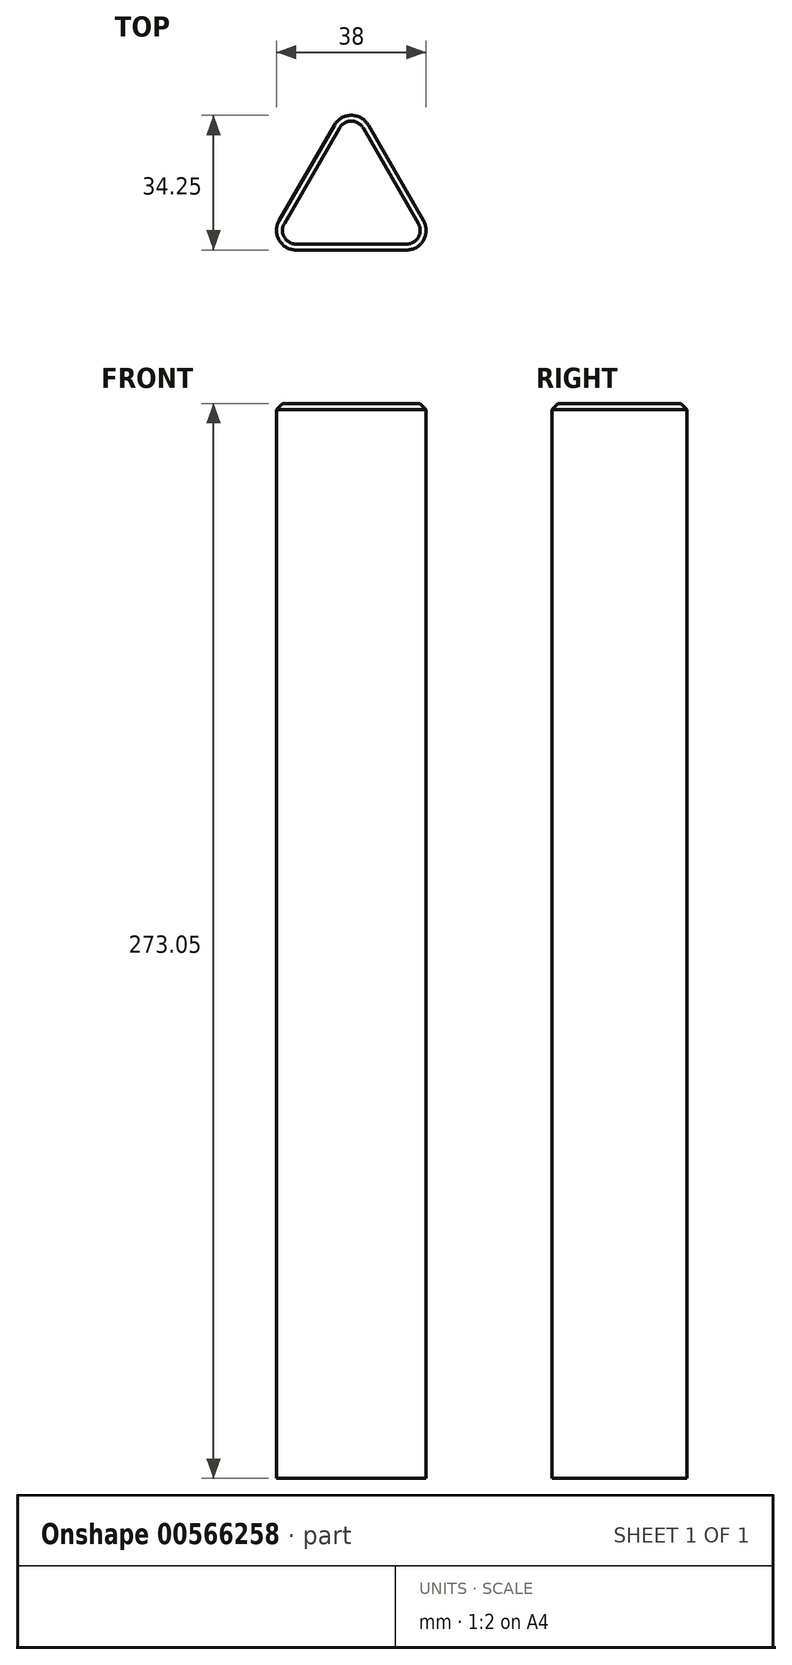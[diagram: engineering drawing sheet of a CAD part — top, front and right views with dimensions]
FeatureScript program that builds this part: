
annotation { "Feature Type Name" : "Feature", "Feature Type Description" : "" }
export const myFeature = defineFeature(function(context is Context, id is Id, definition is map)
    precondition{}
    {
        {
            assignVariable(context, id + "F0", {"variableType" : VariableType.LENGTH, "name" : "height1", "lengthValue" : 273.05 * mm});
        }
        {
            var Q0;
            Q0=qCreatedBy(makeId("Top.planeOp"),FACE);
            var sketch = newSketch(context, id + "F1", { "sketchPlane" : qUnion([Q0])});
            skLineSegment(sketch, "E0", {"start": v(4.33, 18.67) * mm, "end": v(18.33, -5.58) * mm});
            skLineSegment(sketch, "E1", {"start": v(14, -13.08) * mm, "end": v(-14, -13.08) * mm});
            skLineSegment(sketch, "E2", {"start": v(-18.33, -5.58) * mm, "end": v(-4.33, 18.67) * mm});
            skCircle(sketch, "E3", {"center": v(0, 0) * mm, "radius": 13.08 * mm, "construction": true});
            skPoint(sketch, "E4.visualSharp", {"position": v(0, 26.17) * mm});
            skArc(sketch, "E4.filletArc", {"start": v(4.33, 18.67) * mm, "mid": v(0, 21.17) * mm, "end": v(-4.33, 18.67) * mm});
            skPoint(sketch, "E5.visualSharp", {"position": v(22.66, -13.08) * mm});
            skArc(sketch, "E5.filletArc", {"start": v(14, -13.08) * mm, "mid": v(18.33, -10.58) * mm, "end": v(18.33, -5.58) * mm});
            skPoint(sketch, "E6.visualSharp", {"position": v(-22.66, -13.08) * mm});
            skArc(sketch, "E6.filletArc", {"start": v(-18.33, -5.58) * mm, "mid": v(-18.33, -10.58) * mm, "end": v(-14, -13.08) * mm});
            skLineSegment(sketch, "E7", {"start": v(2.5, 20.5) * mm, "end": v(-11.08, 28.33) * mm, "construction": true});
            skLineSegment(sketch, "E8", {"start": v(-16.5, -12.41) * mm, "end": v(-30.08, -4.58) * mm, "construction": true});
            skLineSegment(sketch, "E9", {"start": v(-11.08, 28.33) * mm, "end": v(-30.08, -4.58) * mm, "construction": true});
            skSolve(sketch);
        }
        {
            var Q0;
            Q0=makeQuery(id+"F1.imprint","IMPRINT",FACE,{"disambiguationData":[TD([[makeQuery(id+"F1.imprint","IMPRINT",EDGE,{"derivedFrom":sQuery(id+"F1.wireOp",EDGE,"E0")}),-1.0]])]});
            extrude(context, id + "F2", {"entities" : qUnion([Q0]), "depth" : getVariable(context, 'height1'), "offsetDistance" : 25 * mm});
        }
        {
            var Q0;
            Q0=makeQuery(id+"F2.opExtrude","CAP_FACE",FACE,{"disambiguationData":[OSD([sQuery(id+"F1.wireOp",EDGE,"E0"),sQuery(id+"F1.wireOp",EDGE,"E1"),sQuery(id+"F1.wireOp",EDGE,"E2"),sQuery(id+"F1.wireOp",EDGE,"E4.filletArc"),sQuery(id+"F1.wireOp",EDGE,"E5.filletArc"),sQuery(id+"F1.wireOp",EDGE,"E6.filletArc")])],"isStart":false});
            chamfer(context, id + "F3", {"entities" : qUnion([Q0]), "width" : 1.5 * mm, "tangentPropagation" : true});
        }
    });
